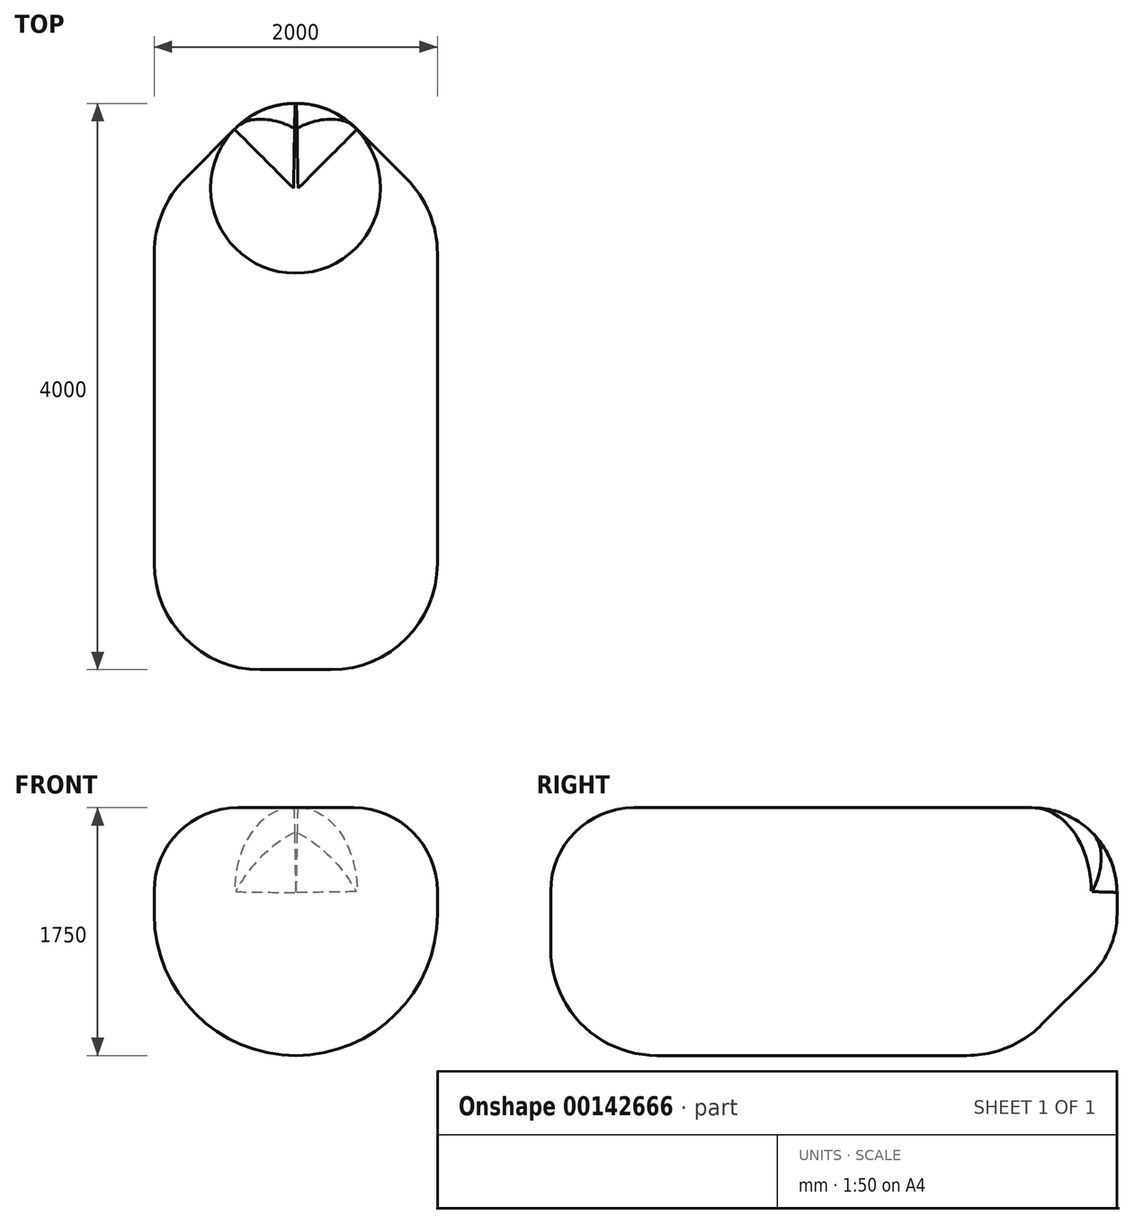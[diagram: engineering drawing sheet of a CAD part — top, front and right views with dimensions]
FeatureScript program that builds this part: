
annotation { "Feature Type Name" : "Feature", "Feature Type Description" : "" }
export const myFeature = defineFeature(function(context is Context, id is Id, definition is map)
    precondition{}
    {
        {
            var Q0;
            Q0=qCreatedBy(makeId("Right.planeOp"),FACE);
            var sketch = newSketch(context, id + "F0", { "sketchPlane" : qUnion([Q0])});
            skLineSegment(sketch, "E0.bottom", {"start": v(-1995, -875) * mm, "end": v(2000, -875) * mm});
            skLineSegment(sketch, "E0.top", {"start": v(-2000, 875) * mm, "end": v(2000, 875) * mm});
            skLineSegment(sketch, "E0.left", {"start": v(-2000, -870) * mm, "end": v(-2000, 875) * mm});
            skLineSegment(sketch, "E0.right", {"start": v(2000, -875) * mm, "end": v(2000, 875) * mm});
            skPoint(sketch, "E0.middle", {"position": v(0, 0) * mm});
            skPoint(sketch, "E1.visualSharp", {"position": v(-2000, -875) * mm});
            skArc(sketch, "E1.filletArc", {"start": v(-2000, -870) * mm, "mid": v(-1998.54, -873.54) * mm, "end": v(-1995, -875) * mm});
            skSolve(sketch);
        }
        {
            var Q0;
            Q0 = qSketchRegion(id + "F0", true);
            extrude(context, id + "F1", {"entities" : qUnion([Q0]), "endBound" : BoundingType.SYMMETRIC, "depth" : 2000 * mm});
        }
        {
            var Q0;
            Q0=makeQuery(id+"F1.opExtrude","CAP_EDGE",EDGE,{"disambiguationData":[OSD([sQuery(id+"F0.wireOp",EDGE,"E0.bottom")])],"isStart":false});
            var Q1;
            Q1=makeQuery(id+"F1.opExtrude","CAP_EDGE",EDGE,{"disambiguationData":[OSD([sQuery(id+"F0.wireOp",EDGE,"E0.bottom")])],"isStart":true});
            fillet(context, id + "F2", {"entities" : qUnion([Q0, Q1]), "radius" : 1000 * mm, "allowEdgeOverflow" : false});
        }
        {
            var Q0;
            Q0=makeQuery(id+"F2.opFillet","BLEND_EDGE",EDGE,{"blendedFrom":[makeQuery(id+"F1.opExtrude","CAP_EDGE",EDGE,{"disambiguationData":[OSD([sQuery(id+"F0.wireOp",EDGE,"E0.bottom")])],"isStart":false}),makeQuery(id+"F1.opExtrude","SWEPT_FACE",FACE,{"disambiguationData":[OSD([sQuery(id+"F0.wireOp",EDGE,"E0.left")])]})],"blendedInto":[makeQuery(id+"F1.opExtrude","SWEPT_FACE",FACE,{"disambiguationData":[OSD([sQuery(id+"F0.wireOp",EDGE,"E0.left")])]})]});
            var Q1;
            Q1=makeQuery(id+"F1.opExtrude","CAP_EDGE",EDGE,{"disambiguationData":[OSD([sQuery(id+"F0.wireOp",EDGE,"E0.left")])],"isStart":false});
            var Q2;
            Q2=makeQuery(id+"F1.opExtrude","CAP_EDGE",EDGE,{"disambiguationData":[OSD([sQuery(id+"F0.wireOp",EDGE,"E0.left")])],"isStart":true});
            var Q3;
            Q3=makeQuery(id+"F2.opFillet","BLEND_EDGE",EDGE,{"blendedFrom":[makeQuery(id+"F1.opExtrude","CAP_EDGE",EDGE,{"disambiguationData":[OSD([sQuery(id+"F0.wireOp",EDGE,"E0.bottom")])],"isStart":true}),makeQuery(id+"F1.opExtrude","SWEPT_FACE",FACE,{"disambiguationData":[OSD([sQuery(id+"F0.wireOp",EDGE,"E0.left")])]})],"blendedInto":[makeQuery(id+"F1.opExtrude","SWEPT_FACE",FACE,{"disambiguationData":[OSD([sQuery(id+"F0.wireOp",EDGE,"E0.left")])]})]});
            fillet(context, id + "F3", {"entities" : qUnion([Q0, Q1, Q2, Q3]), "radius" : 750 * mm, "tangentPropagation" : true, "allowEdgeOverflow" : false});
        }
        {
            var Q0;
            Q0=makeQuery(id+"F2.opFillet","BLEND_EDGE",EDGE,{"blendedFrom":[makeQuery(id+"F1.opExtrude","CAP_EDGE",EDGE,{"disambiguationData":[OSD([sQuery(id+"F0.wireOp",EDGE,"E0.bottom")])],"isStart":false}),makeQuery(id+"F1.opExtrude","SWEPT_FACE",FACE,{"disambiguationData":[OSD([sQuery(id+"F0.wireOp",EDGE,"E0.right")])]})],"blendedInto":[makeQuery(id+"F1.opExtrude","SWEPT_FACE",FACE,{"disambiguationData":[OSD([sQuery(id+"F0.wireOp",EDGE,"E0.right")])]})]});
            var Q1;
            Q1=makeQuery(id+"F1.opExtrude","CAP_EDGE",EDGE,{"disambiguationData":[OSD([sQuery(id+"F0.wireOp",EDGE,"E0.right")])],"isStart":false});
            var Q2;
            Q2=makeQuery(id+"F1.opExtrude","CAP_EDGE",EDGE,{"disambiguationData":[OSD([sQuery(id+"F0.wireOp",EDGE,"E0.right")])],"isStart":true});
            chamfer(context, id + "F4", {"entities" : qUnion([Q0, Q1, Q2]), "width" : 750 * mm, "tangentPropagation" : true});
        }
        {
            var Q0;
            Q0=makeQuery(id+"F1.opExtrude","SWEPT_FACE",FACE,{"disambiguationData":[OSD([sQuery(id+"F0.wireOp",EDGE,"E0.right")])]});
            fillet(context, id + "F5", {"entities" : qUnion([Q0]), "radius" : 600 * mm, "allowEdgeOverflow" : false});
        }
        {
            var Q0;
            Q0=makeQuery(id+"F1.opExtrude","SWEPT_FACE",FACE,{"disambiguationData":[OSD([sQuery(id+"F0.wireOp",EDGE,"E0.top")])]});
            fillet(context, id + "F6", {"entities" : qUnion([Q0]), "radius" : 590 * mm, "tangentPropagation" : true, "allowEdgeOverflow" : false});
        }
        {
            var Q0;
            {var subQ0=sQuery(id+"F0.wireOp",EDGE,"E0.bottom");Q0=makeQuery(id+"F4.opChamfer","BLEND_EDGE",EDGE,{"blendedFrom":[makeQuery(id+"F2.opFillet","BLEND_EDGE",EDGE,{"blendedFrom":[makeQuery(id+"F1.opExtrude","CAP_EDGE",EDGE,{"disambiguationData":[OSD([subQ0])],"isStart":false}),makeQuery(id+"F1.opExtrude","SWEPT_FACE",FACE,{"disambiguationData":[OSD([sQuery(id+"F0.wireOp",EDGE,"E0.right")])]})],"blendedInto":[makeQuery(id+"F1.opExtrude","SWEPT_FACE",FACE,{"disambiguationData":[OSD([sQuery(id+"F0.wireOp",EDGE,"E0.right")])]})]}),makeQuery(id+"F2.opFillet","BLEND_FACE",FACE,{"disambiguationData":[OSD([subQ0])]})],"blendedInto":[makeQuery(id+"F2.opFillet","BLEND_FACE",FACE,{"disambiguationData":[OSD([subQ0])]})]});}
            var Q1;
            {var subQ0=sQuery(id+"F0.wireOp",EDGE,"E0.top");Q1=makeQuery(id+"F6.opFillet","BLEND_EDGE",EDGE,{"blendedFrom":[makeQuery(id+"F1.opExtrude","CAP_EDGE",EDGE,{"disambiguationData":[OSD([subQ0])],"isStart":false}),makeQuery(id+"F4.opChamfer","BLEND_EDGE",EDGE,{"blendedFrom":[makeQuery(id+"F1.opExtrude","CAP_EDGE",EDGE,{"disambiguationData":[OSD([sQuery(id+"F0.wireOp",EDGE,"E0.right")])],"isStart":false}),makeQuery(id+"F1.opExtrude","SWEPT_FACE",FACE,{"disambiguationData":[OSD([subQ0])]})],"blendedInto":[makeQuery(id+"F1.opExtrude","SWEPT_FACE",FACE,{"disambiguationData":[OSD([subQ0])]})]})],"blendedInto":[]});}
            var Q2;
            {var subQ0=sQuery(id+"F0.wireOp",EDGE,"E0.right");Q2=makeQuery(id+"F4.opChamfer","BLEND_EDGE",EDGE,{"blendedFrom":[makeQuery(id+"F1.opExtrude","CAP_EDGE",EDGE,{"disambiguationData":[OSD([subQ0])],"isStart":false}),makeQuery(id+"F1.opExtrude","CAP_FACE",FACE,{"disambiguationData":[OSD([sQuery(id+"F0.wireOp",EDGE,"E0.bottom"),sQuery(id+"F0.wireOp",EDGE,"E0.top"),sQuery(id+"F0.wireOp",EDGE,"E0.left"),subQ0,sQuery(id+"F0.wireOp",EDGE,"E1.filletArc")])],"isStart":false})],"blendedInto":[makeQuery(id+"F1.opExtrude","CAP_FACE",FACE,{"disambiguationData":[OSD([sQuery(id+"F0.wireOp",EDGE,"E0.bottom"),sQuery(id+"F0.wireOp",EDGE,"E0.top"),sQuery(id+"F0.wireOp",EDGE,"E0.left"),subQ0,sQuery(id+"F0.wireOp",EDGE,"E1.filletArc")])],"isStart":false})]});}
            var Q3;
            {var subQ0=sQuery(id+"F0.wireOp",EDGE,"E0.right");Q3=makeQuery(id+"F4.opChamfer","BLEND_EDGE",EDGE,{"blendedFrom":[makeQuery(id+"F1.opExtrude","CAP_EDGE",EDGE,{"disambiguationData":[OSD([subQ0])],"isStart":true}),makeQuery(id+"F1.opExtrude","CAP_FACE",FACE,{"disambiguationData":[OSD([sQuery(id+"F0.wireOp",EDGE,"E0.bottom"),sQuery(id+"F0.wireOp",EDGE,"E0.top"),sQuery(id+"F0.wireOp",EDGE,"E0.left"),subQ0,sQuery(id+"F0.wireOp",EDGE,"E1.filletArc")])],"isStart":true})],"blendedInto":[makeQuery(id+"F1.opExtrude","CAP_FACE",FACE,{"disambiguationData":[OSD([sQuery(id+"F0.wireOp",EDGE,"E0.bottom"),sQuery(id+"F0.wireOp",EDGE,"E0.top"),sQuery(id+"F0.wireOp",EDGE,"E0.left"),subQ0,sQuery(id+"F0.wireOp",EDGE,"E1.filletArc")])],"isStart":true})]});}
            var Q4;
            {var subQ0=sQuery(id+"F0.wireOp",EDGE,"E0.top");Q4=makeQuery(id+"F6.opFillet","BLEND_EDGE",EDGE,{"blendedFrom":[makeQuery(id+"F1.opExtrude","CAP_EDGE",EDGE,{"disambiguationData":[OSD([subQ0])],"isStart":true}),makeQuery(id+"F4.opChamfer","BLEND_EDGE",EDGE,{"blendedFrom":[makeQuery(id+"F1.opExtrude","CAP_EDGE",EDGE,{"disambiguationData":[OSD([sQuery(id+"F0.wireOp",EDGE,"E0.right")])],"isStart":true}),makeQuery(id+"F1.opExtrude","SWEPT_FACE",FACE,{"disambiguationData":[OSD([subQ0])]})],"blendedInto":[makeQuery(id+"F1.opExtrude","SWEPT_FACE",FACE,{"disambiguationData":[OSD([subQ0])]})]})],"blendedInto":[]});}
            var Q5;
            {var subQ0=makeQuery(id+"F1.opExtrude","SWEPT_FACE",FACE,{"disambiguationData":[OSD([sQuery(id+"F0.wireOp",EDGE,"E0.top")])]});Q5=makeQuery(id+"F6.opFillet","BLEND_EDGE",EDGE,{"blendedFrom":[makeQuery(id+"F4.opChamfer","BLEND_EDGE",EDGE,{"blendedFrom":[makeQuery(id+"F1.opExtrude","CAP_EDGE",EDGE,{"disambiguationData":[OSD([sQuery(id+"F0.wireOp",EDGE,"E0.right")])],"isStart":false}),subQ0],"blendedInto":[subQ0]}),subQ0],"blendedInto":[subQ0]});}
            var Q6;
            {var subQ0=makeQuery(id+"F1.opExtrude","SWEPT_FACE",FACE,{"disambiguationData":[OSD([sQuery(id+"F0.wireOp",EDGE,"E0.top")])]});Q6=makeQuery(id+"F6.opFillet","BLEND_EDGE",EDGE,{"blendedFrom":[makeQuery(id+"F4.opChamfer","BLEND_EDGE",EDGE,{"blendedFrom":[makeQuery(id+"F1.opExtrude","CAP_EDGE",EDGE,{"disambiguationData":[OSD([sQuery(id+"F0.wireOp",EDGE,"E0.right")])],"isStart":true}),subQ0],"blendedInto":[subQ0]}),subQ0],"blendedInto":[subQ0]});}
            fillet(context, id + "F7", {"entities" : qUnion([Q0, Q1, Q2, Q3, Q4, Q5, Q6]), "radius" : 750 * mm, "tangentPropagation" : true, "allowEdgeOverflow" : false});
        }
    });
